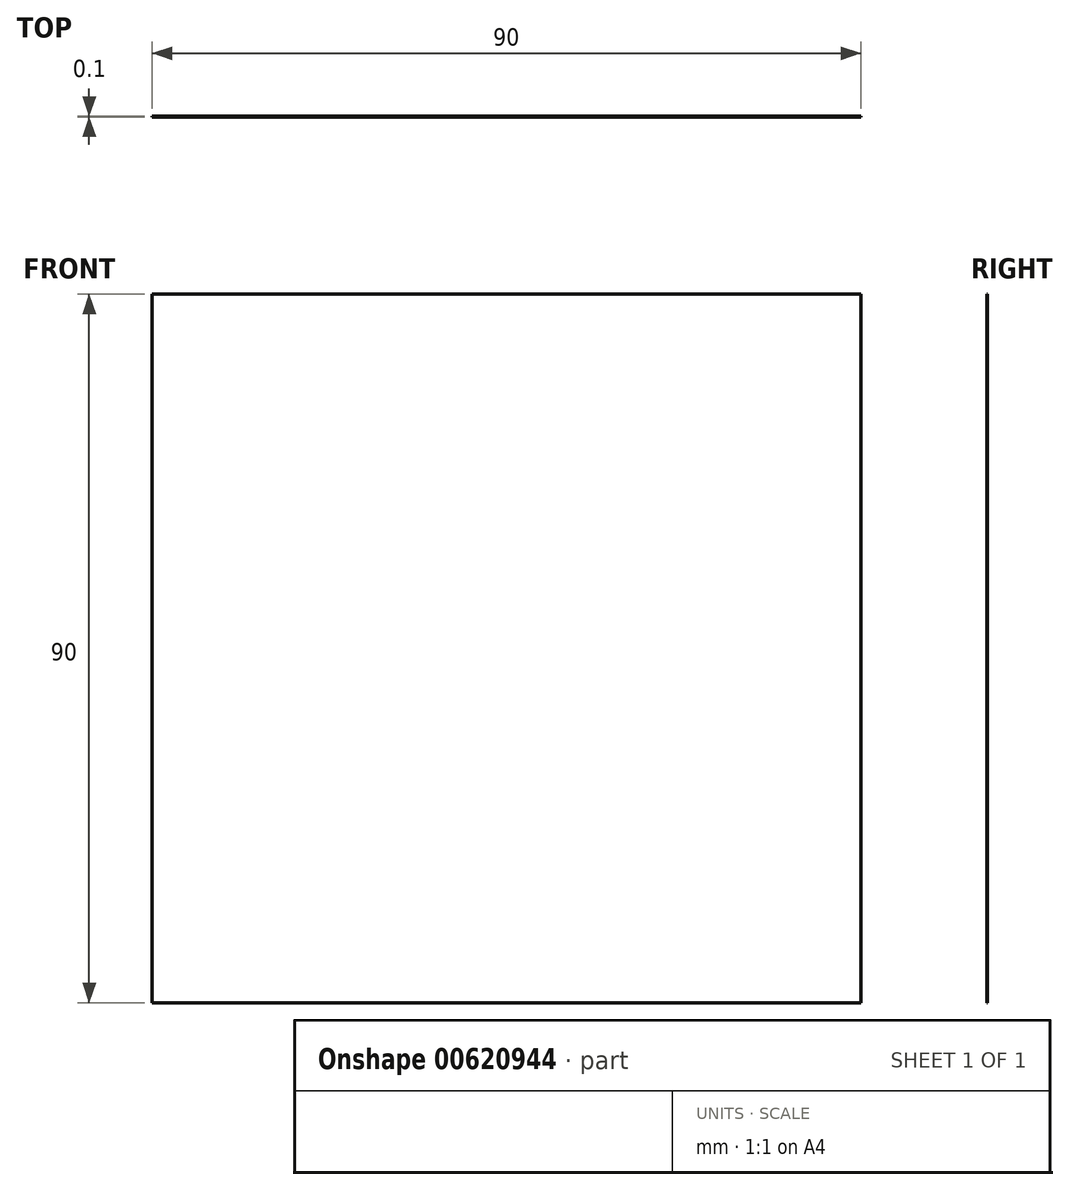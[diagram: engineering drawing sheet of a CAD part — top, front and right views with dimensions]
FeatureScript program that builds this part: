
annotation { "Feature Type Name" : "Feature", "Feature Type Description" : "" }
export const myFeature = defineFeature(function(context is Context, id is Id, definition is map)
    precondition{}
    {
        {
            var Q0;
            Q0=qCreatedBy(makeId("Front.planeOp"),FACE);
            var sketch = newSketch(context, id + "F0", { "sketchPlane" : qUnion([Q0])});
            skLineSegment(sketch, "E0.bottom", {"start": v(-51.06, 62.17) * mm, "end": v(38.94, 62.17) * mm});
            skLineSegment(sketch, "E0.top", {"start": v(-51.06, -27.83) * mm, "end": v(38.94, -27.83) * mm});
            skLineSegment(sketch, "E0.left", {"start": v(-51.06, 62.17) * mm, "end": v(-51.06, -27.83) * mm});
            skLineSegment(sketch, "E0.right", {"start": v(38.94, 62.17) * mm, "end": v(38.94, -27.83) * mm});
            skSolve(sketch);
        }
        {
            var Q0;
            Q0 = qSketchRegion(id + "F0", true);
            extrude(context, id + "F1", {"entities" : qUnion([Q0]), "depth" : 0.1 * mm, "offsetDistance" : 25 * mm});
        }
    });
